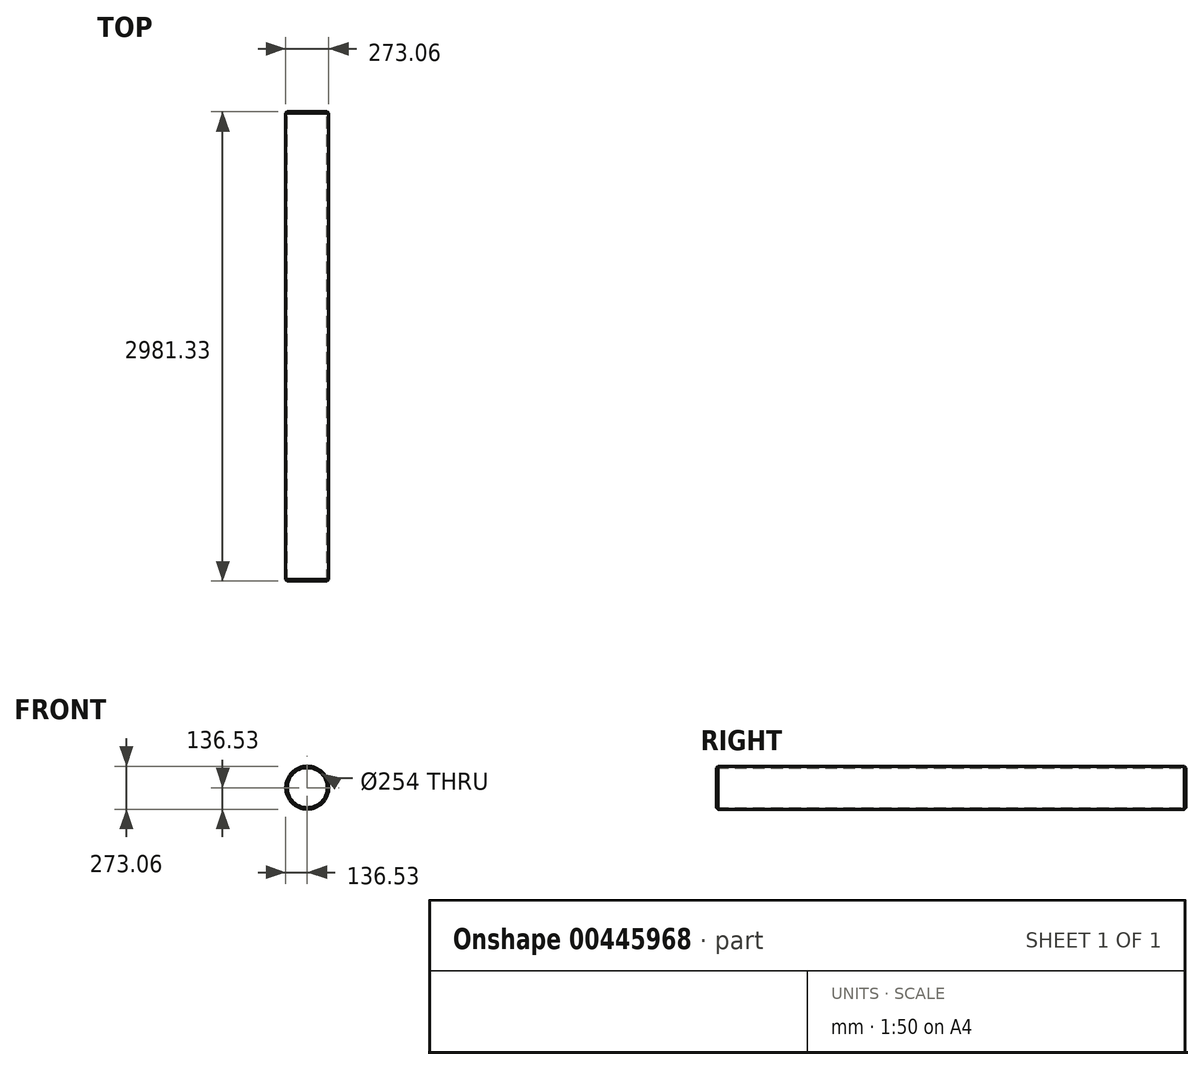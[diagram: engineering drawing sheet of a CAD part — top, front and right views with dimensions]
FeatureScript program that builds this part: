
annotation { "Feature Type Name" : "Feature", "Feature Type Description" : "" }
export const myFeature = defineFeature(function(context is Context, id is Id, definition is map)
    precondition{}
    {
        {
            var Q0;
            Q0=qCreatedBy(makeId("Front.planeOp"),FACE);
            var sketch = newSketch(context, id + "F0", { "sketchPlane" : qUnion([Q0])});
            skCircle(sketch, "E0", {"center": v(0, 0) * mm, "radius": 136.53 * mm});
            skCircle(sketch, "E1", {"center": v(0, 0) * mm, "radius": 127 * mm});
            skSolve(sketch);
        }
        {
            var Q0;
            Q0 = qSketchRegion(id + "F0", true);
            extrude(context, id + "F1", {"entities" : qUnion([Q0]), "depth" : 2981.32 * mm, "offsetDistance" : 25.4 * mm});
        }
        {
            var Q0;
            Q0=makeQuery(id+"F1.opExtrude","CAP_EDGE",EDGE,{"disambiguationData":[OSD([sQuery(id+"F0.wireOp",EDGE,"E0")])],"isStart":true});
            var Q1;
            Q1=makeQuery(id+"F1.opExtrude","CAP_EDGE",EDGE,{"disambiguationData":[OSD([sQuery(id+"F0.wireOp",EDGE,"E0")])],"isStart":false});
            chamfer(context, id + "F2", {"entities" : qUnion([Q0, Q1]), "width" : 9.52 * mm, "tangentPropagation" : true});
        }
    });
